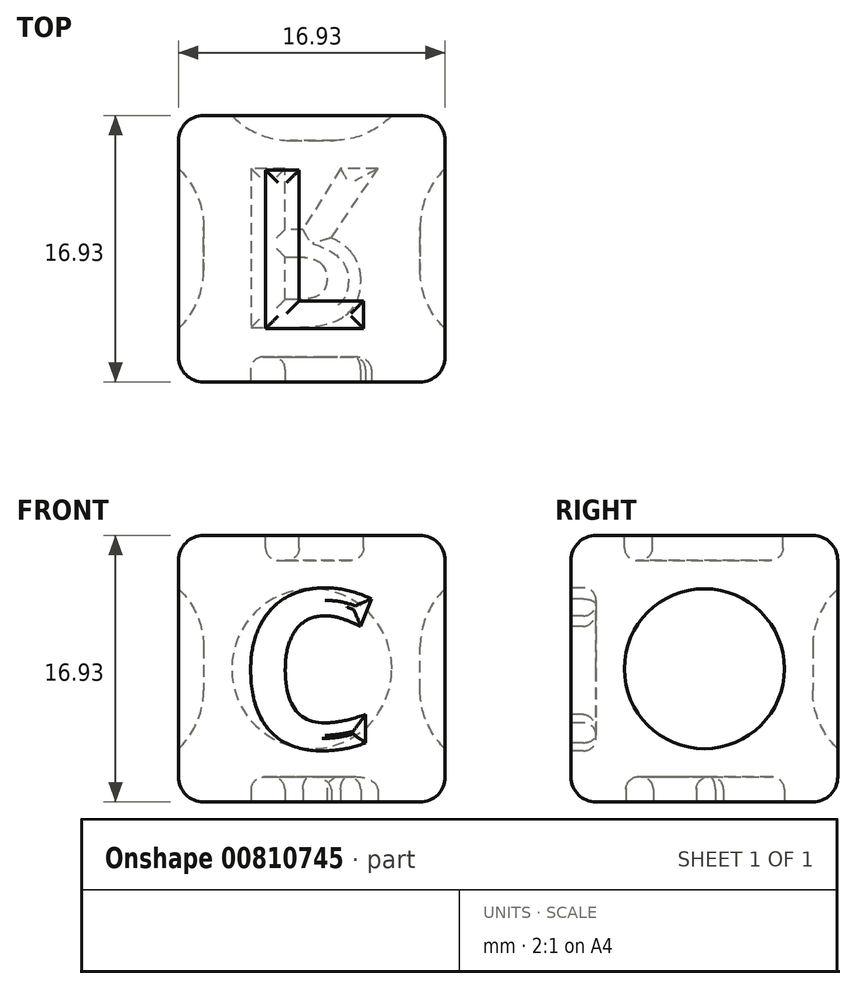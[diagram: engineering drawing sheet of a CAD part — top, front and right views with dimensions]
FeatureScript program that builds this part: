
annotation { "Feature Type Name" : "Feature", "Feature Type Description" : "" }
export const myFeature = defineFeature(function(context is Context, id is Id, definition is map)
    precondition{}
    {
        {
            var Q0;
            Q0=qCreatedBy(makeId("Top.planeOp"),FACE);
            var sketch = newSketch(context, id + "F0", { "sketchPlane" : qUnion([Q0])});
            skLineSegment(sketch, "E0.bottom", {"start": v(0, 0) * mm, "end": v(16.93, 0) * mm});
            skLineSegment(sketch, "E0.top", {"start": v(0, 16.93) * mm, "end": v(16.93, 16.93) * mm});
            skLineSegment(sketch, "E0.left", {"start": v(0, 0) * mm, "end": v(0, 16.93) * mm});
            skLineSegment(sketch, "E0.right", {"start": v(16.93, 0) * mm, "end": v(16.93, 16.93) * mm});
            skSolve(sketch);
        }
        {
            var Q0;
            Q0 = qSketchRegion(id + "F0", true);
            extrude(context, id + "F1", {"entities" : qUnion([Q0]), "depth" : 16.93 * mm, "offsetDistance" : 25.4 * mm});
        }
        {
            var Q0;
            Q0=makeQuery(id+"F1.opExtrude","CAP_EDGE",EDGE,{"disambiguationData":[OSD([sQuery(id+"F0.wireOp",EDGE,"E0.bottom")])],"isStart":false});
            var Q1;
            Q1=makeQuery(id+"F1.opExtrude","CAP_EDGE",EDGE,{"disambiguationData":[OSD([sQuery(id+"F0.wireOp",EDGE,"E0.left")])],"isStart":false});
            var Q2;
            Q2=makeQuery(id+"F1.opExtrude","CAP_EDGE",EDGE,{"disambiguationData":[OSD([sQuery(id+"F0.wireOp",EDGE,"E0.top")])],"isStart":false});
            var Q3;
            Q3=makeQuery(id+"F1.opExtrude","CAP_EDGE",EDGE,{"disambiguationData":[OSD([sQuery(id+"F0.wireOp",EDGE,"E0.right")])],"isStart":false});
            var Q4;
            Q4=makeQuery(id+"F1.opExtrude","SWEPT_EDGE",EDGE,{"disambiguationData":[OSD([sQuery(id+"F0.wireOp",EDGE,"E0.bottom"),sQuery(id+"F0.wireOp",EDGE,"E0.left")])]});
            var Q5;
            Q5=makeQuery(id+"F1.opExtrude","SWEPT_EDGE",EDGE,{"disambiguationData":[OSD([sQuery(id+"F0.wireOp",EDGE,"E0.top"),sQuery(id+"F0.wireOp",EDGE,"E0.left")])]});
            var Q6;
            Q6=makeQuery(id+"F1.opExtrude","SWEPT_EDGE",EDGE,{"disambiguationData":[OSD([sQuery(id+"F0.wireOp",EDGE,"E0.bottom"),sQuery(id+"F0.wireOp",EDGE,"E0.right")])]});
            var Q7;
            Q7=makeQuery(id+"F1.opExtrude","SWEPT_EDGE",EDGE,{"disambiguationData":[OSD([sQuery(id+"F0.wireOp",EDGE,"E0.top"),sQuery(id+"F0.wireOp",EDGE,"E0.right")])]});
            var Q8;
            Q8=makeQuery(id+"F1.opExtrude","CAP_EDGE",EDGE,{"disambiguationData":[OSD([sQuery(id+"F0.wireOp",EDGE,"E0.right")])],"isStart":true});
            var Q9;
            Q9=makeQuery(id+"F1.opExtrude","CAP_EDGE",EDGE,{"disambiguationData":[OSD([sQuery(id+"F0.wireOp",EDGE,"E0.left")])],"isStart":true});
            var Q10;
            Q10=makeQuery(id+"F1.opExtrude","CAP_EDGE",EDGE,{"disambiguationData":[OSD([sQuery(id+"F0.wireOp",EDGE,"E0.bottom")])],"isStart":true});
            var Q11;
            Q11=makeQuery(id+"F1.opExtrude","CAP_EDGE",EDGE,{"disambiguationData":[OSD([sQuery(id+"F0.wireOp",EDGE,"E0.top")])],"isStart":true});
            fillet(context, id + "F2", {"entities" : qUnion([Q0, Q1, Q2, Q3, Q4, Q5, Q6, Q7, Q8, Q9, Q10, Q11]), "radius" : 1.59 * mm, "tangentPropagation" : true, "allowEdgeOverflow" : false});
        }
        {
            var Q0;
            Q0=makeQuery(id+"F1.opExtrude","CAP_FACE",FACE,{"disambiguationData":[OSD([sQuery(id+"F0.wireOp",EDGE,"E0.bottom"),sQuery(id+"F0.wireOp",EDGE,"E0.top"),sQuery(id+"F0.wireOp",EDGE,"E0.left"),sQuery(id+"F0.wireOp",EDGE,"E0.right")])],"isStart":false});
            var sketch = newSketch(context, id + "F3", { "sketchPlane" : qUnion([Q0])});
            skText(sketch, "E1", { "text": "L", "fontName": "NotoSans-Bold.ttf"});
            skLineSegment(sketch, "E2", {"start": v(1.59, 15.35) * mm, "end": v(15.35, 1.59) * mm, "construction": true});
            skPoint(sketch, "E3", {"position": v(8.47, 8.47) * mm});
            const initialGuessF3  = {"E1": [0.00426, 0.00339, 1, 0, 0.01016]};
            skSetInitialGuess(sketch, initialGuessF3);
            skSolve(sketch);
        }
        {
            var Q0;
            Q0 = qSketchRegion(id + "F3", true);
            extrude(context, id + "F4", {"entities" : qUnion([Q0]), "operationType" : NewBodyOperationType.REMOVE, "oppositeDirection" : true, "depth" : 1.59 * mm, "offsetDistance" : 25.4 * mm});
        }
        {
            var Q0;
            Q0=makeQuery(id+"F1.opExtrude","SWEPT_FACE",FACE,{"disambiguationData":[OSD([sQuery(id+"F0.wireOp",EDGE,"E0.bottom")])]});
            var sketch = newSketch(context, id + "F5", { "sketchPlane" : qUnion([Q0])});
            skText(sketch, "E4", { "text": "C", "fontName": "NotoSans-Bold.ttf"});
            skLineSegment(sketch, "E5", {"start": v(1.59, 15.35) * mm, "end": v(15.35, 1.59) * mm, "construction": true});
            skPoint(sketch, "E6", {"position": v(8.47, 8.47) * mm});
            const initialGuessF5  = {"E4": [0.00376, 0.00339, 1, 0, 0.01016]};
            skSetInitialGuess(sketch, initialGuessF5);
            skSolve(sketch);
        }
        {
            var Q0;
            Q0 = qSketchRegion(id + "F5", true);
            extrude(context, id + "F6", {"entities" : qUnion([Q0]), "operationType" : NewBodyOperationType.REMOVE, "oppositeDirection" : true, "depth" : 1.59 * mm, "offsetDistance" : 25.4 * mm});
        }
        {
            var Q0;
            Q0=makeQuery(id+"F1.opExtrude","CAP_FACE",FACE,{"disambiguationData":[OSD([sQuery(id+"F0.wireOp",EDGE,"E0.bottom"),sQuery(id+"F0.wireOp",EDGE,"E0.top"),sQuery(id+"F0.wireOp",EDGE,"E0.left"),sQuery(id+"F0.wireOp",EDGE,"E0.right")])],"isStart":true});
            var sketch = newSketch(context, id + "F7", { "sketchPlane" : qUnion([Q0])});
            skText(sketch, "E7", { "text": "R", "fontName": "NotoSans-Bold.ttf"});
            skLineSegment(sketch, "E8", {"start": v(1.59, -1.59) * mm, "end": v(15.35, -15.35) * mm, "construction": true});
            skPoint(sketch, "E9", {"position": v(8.47, -8.47) * mm});
            const initialGuessF7  = {"E7": [0.00335, -0.01355, 1, 0, 0.01016]};
            skSetInitialGuess(sketch, initialGuessF7);
            skSolve(sketch);
        }
        {
            var Q0;
            Q0 = qSketchRegion(id + "F7", true);
            extrude(context, id + "F8", {"entities" : qUnion([Q0]), "operationType" : NewBodyOperationType.REMOVE, "oppositeDirection" : true, "depth" : 1.59 * mm, "offsetDistance" : 25.4 * mm});
        }
        {
            var Q0;
            Q0=makeQuery(id+"F1.opExtrude","SWEPT_FACE",FACE,{"disambiguationData":[OSD([sQuery(id+"F0.wireOp",EDGE,"E0.left")])]});
            var sketch = newSketch(context, id + "F9", { "sketchPlane" : qUnion([Q0])});
            skLineSegment(sketch, "E10", {"start": v(-15.35, 15.35) * mm, "end": v(-1.59, 1.59) * mm, "construction": true});
            skCircle(sketch, "E11", {"center": v(-8.47, 8.47) * mm, "radius": 5.08 * mm});
            skSolve(sketch);
        }
        {
            var Q0;
            Q0 = qSketchRegion(id + "F9", true);
            extrude(context, id + "F10", {"entities" : qUnion([Q0]), "operationType" : NewBodyOperationType.REMOVE, "oppositeDirection" : true, "depth" : 1.59 * mm, "offsetDistance" : 25.4 * mm});
        }
        {
            var Q0;
            Q0=makeQuery(id+"F1.opExtrude","SWEPT_FACE",FACE,{"disambiguationData":[OSD([sQuery(id+"F0.wireOp",EDGE,"E0.top")])]});
            var sketch = newSketch(context, id + "F11", { "sketchPlane" : qUnion([Q0])});
            skLineSegment(sketch, "E12", {"start": v(-15.35, 15.35) * mm, "end": v(-1.59, 1.59) * mm, "construction": true});
            skCircle(sketch, "E13", {"center": v(-8.47, 8.47) * mm, "radius": 5.08 * mm});
            skSolve(sketch);
        }
        {
            var Q0;
            Q0 = qSketchRegion(id + "F11", true);
            extrude(context, id + "F12", {"entities" : qUnion([Q0]), "operationType" : NewBodyOperationType.REMOVE, "oppositeDirection" : true, "depth" : 1.59 * mm, "offsetDistance" : 25.4 * mm});
        }
        {
            var Q0;
            Q0=makeQuery(id+"F1.opExtrude","SWEPT_FACE",FACE,{"disambiguationData":[OSD([sQuery(id+"F0.wireOp",EDGE,"E0.right")])]});
            var sketch = newSketch(context, id + "F13", { "sketchPlane" : qUnion([Q0])});
            skLineSegment(sketch, "E14", {"start": v(1.59, 15.35) * mm, "end": v(15.35, 1.59) * mm, "construction": true});
            skCircle(sketch, "E15", {"center": v(8.47, 8.47) * mm, "radius": 5.08 * mm});
            skSolve(sketch);
        }
        {
            var Q0;
            Q0 = qSketchRegion(id + "F13", true);
            extrude(context, id + "F14", {"entities" : qUnion([Q0]), "operationType" : NewBodyOperationType.REMOVE, "oppositeDirection" : true, "depth" : 1.59 * mm, "offsetDistance" : 25.4 * mm});
        }
        {
            var Q0;
            Q0=makeQuery(id+"F4.boolean.opBoolean","COPY",EDGE,{"derivedFrom":makeQuery(id+"F4.opExtrude","CAP_EDGE",EDGE,{"disambiguationData":[OSD([sQuery(id+"F3.wireOp",EDGE,"E1.sketch_text.stroke-2")])],"isStart":false})});
            var Q1;
            Q1=makeQuery(id+"F4.boolean.opBoolean","COPY",EDGE,{"derivedFrom":makeQuery(id+"F4.opExtrude","CAP_EDGE",EDGE,{"disambiguationData":[OSD([sQuery(id+"F3.wireOp",EDGE,"E1.sketch_text.stroke-0")])],"isStart":false})});
            var Q2;
            Q2=makeQuery(id+"F4.boolean.opBoolean","COPY",EDGE,{"derivedFrom":makeQuery(id+"F4.opExtrude","CAP_EDGE",EDGE,{"disambiguationData":[OSD([sQuery(id+"F3.wireOp",EDGE,"E1.sketch_text.stroke-3")])],"isStart":false})});
            var Q3;
            Q3=makeQuery(id+"F4.boolean.opBoolean","COPY",EDGE,{"derivedFrom":makeQuery(id+"F4.opExtrude","CAP_EDGE",EDGE,{"disambiguationData":[OSD([sQuery(id+"F3.wireOp",EDGE,"E1.sketch_text.stroke-5")])],"isStart":false})});
            var Q4;
            Q4=makeQuery(id+"F4.boolean.opBoolean","COPY",EDGE,{"derivedFrom":makeQuery(id+"F4.opExtrude","CAP_EDGE",EDGE,{"disambiguationData":[OSD([sQuery(id+"F3.wireOp",EDGE,"E1.sketch_text.stroke-4")])],"isStart":false})});
            var Q5;
            Q5=makeQuery(id+"F4.boolean.opBoolean","COPY",EDGE,{"derivedFrom":makeQuery(id+"F4.opExtrude","CAP_EDGE",EDGE,{"disambiguationData":[OSD([sQuery(id+"F3.wireOp",EDGE,"E1.sketch_text.stroke-1")])],"isStart":false})});
            var Q6;
            Q6=makeQuery(id+"F6.boolean.opBoolean","COPY",EDGE,{"derivedFrom":makeQuery(id+"F6.opExtrude","CAP_EDGE",EDGE,{"disambiguationData":[OSD([sQuery(id+"F5.wireOp",EDGE,"E4.sketch_text.stroke-10")])],"isStart":false})});
            var Q7;
            Q7=makeQuery(id+"F6.boolean.opBoolean","COPY",EDGE,{"derivedFrom":makeQuery(id+"F6.opExtrude","CAP_EDGE",EDGE,{"disambiguationData":[OSD([sQuery(id+"F5.wireOp",EDGE,"E4.sketch_text.stroke-0")])],"isStart":false})});
            var Q8;
            Q8=makeQuery(id+"F6.boolean.opBoolean","COPY",EDGE,{"derivedFrom":makeQuery(id+"F6.opExtrude","CAP_EDGE",EDGE,{"disambiguationData":[OSD([sQuery(id+"F5.wireOp",EDGE,"E4.sketch_text.stroke-12")])],"isStart":false})});
            var Q9;
            Q9=makeQuery(id+"F6.boolean.opBoolean","COPY",EDGE,{"derivedFrom":makeQuery(id+"F6.opExtrude","CAP_EDGE",EDGE,{"disambiguationData":[OSD([sQuery(id+"F5.wireOp",EDGE,"E4.sketch_text.stroke-4")])],"isStart":false})});
            var Q10;
            Q10=makeQuery(id+"F8.boolean.opBoolean","COPY",EDGE,{"derivedFrom":makeQuery(id+"F8.opExtrude","CAP_EDGE",EDGE,{"disambiguationData":[OSD([sQuery(id+"F7.wireOp",EDGE,"E7.sketch_text.stroke-11")])],"isStart":false})});
            var Q11;
            Q11=makeQuery(id+"F8.boolean.opBoolean","COPY",EDGE,{"derivedFrom":makeQuery(id+"F8.opExtrude","CAP_EDGE",EDGE,{"disambiguationData":[OSD([sQuery(id+"F7.wireOp",EDGE,"E7.sketch_text.stroke-15")])],"isStart":false})});
            var Q12;
            Q12=makeQuery(id+"F8.boolean.opBoolean","COPY",EDGE,{"derivedFrom":makeQuery(id+"F8.opExtrude","CAP_EDGE",EDGE,{"disambiguationData":[OSD([sQuery(id+"F7.wireOp",EDGE,"E7.sketch_text.stroke-1")])],"isStart":false})});
            var Q13;
            Q13=makeQuery(id+"F8.boolean.opBoolean","COPY",EDGE,{"derivedFrom":makeQuery(id+"F8.opExtrude","CAP_EDGE",EDGE,{"disambiguationData":[OSD([sQuery(id+"F7.wireOp",EDGE,"E7.sketch_text.stroke-6")])],"isStart":false})});
            var Q14;
            Q14=makeQuery(id+"F8.boolean.opBoolean","COPY",EDGE,{"derivedFrom":makeQuery(id+"F8.opExtrude","CAP_EDGE",EDGE,{"disambiguationData":[OSD([sQuery(id+"F7.wireOp",EDGE,"E7.sketch_text.stroke-9")])],"isStart":false})});
            var Q15;
            Q15=makeQuery(id+"F8.boolean.opBoolean","COPY",EDGE,{"derivedFrom":makeQuery(id+"F8.opExtrude","CAP_EDGE",EDGE,{"disambiguationData":[OSD([sQuery(id+"F7.wireOp",EDGE,"E7.sketch_text.stroke-8")])],"isStart":false})});
            var Q16;
            Q16=makeQuery(id+"F8.boolean.opBoolean","COPY",EDGE,{"derivedFrom":makeQuery(id+"F8.opExtrude","CAP_EDGE",EDGE,{"disambiguationData":[OSD([sQuery(id+"F7.wireOp",EDGE,"E7.sketch_text.stroke-7")])],"isStart":false})});
            var Q17;
            Q17=makeQuery(id+"F8.boolean.opBoolean","COPY",EDGE,{"derivedFrom":makeQuery(id+"F8.opExtrude","CAP_EDGE",EDGE,{"disambiguationData":[OSD([sQuery(id+"F7.wireOp",EDGE,"E7.sketch_text.stroke-16")])],"isStart":false})});
            var Q18;
            Q18=makeQuery(id+"F8.boolean.opBoolean","COPY",EDGE,{"derivedFrom":makeQuery(id+"F8.opExtrude","CAP_EDGE",EDGE,{"disambiguationData":[OSD([sQuery(id+"F7.wireOp",EDGE,"E7.sketch_text.stroke-17")])],"isStart":false})});
            var Q19;
            Q19=makeQuery(id+"F8.boolean.opBoolean","COPY",EDGE,{"derivedFrom":makeQuery(id+"F8.opExtrude","CAP_EDGE",EDGE,{"disambiguationData":[OSD([sQuery(id+"F7.wireOp",EDGE,"E7.sketch_text.stroke-18")])],"isStart":false})});
            fillet(context, id + "F15", {"entities" : qUnion([Q0, Q1, Q2, Q3, Q4, Q5, Q6, Q7, Q8, Q9, Q10, Q11, Q12, Q13, Q14, Q15, Q16, Q17, Q18, Q19]), "radius" : 0.8 * mm, "tangentPropagation" : true, "allowEdgeOverflow" : false});
        }
        {
            var Q0;
            Q0=makeQuery(id+"F12.boolean.opBoolean","COPY",EDGE,{"derivedFrom":makeQuery(id+"F12.opExtrude","CAP_EDGE",EDGE,{"disambiguationData":[OSD([sQuery(id+"F11.wireOp",EDGE,"E13")])],"isStart":false})});
            var Q1;
            Q1=makeQuery(id+"F14.boolean.opBoolean","COPY",EDGE,{"derivedFrom":makeQuery(id+"F14.opExtrude","CAP_EDGE",EDGE,{"disambiguationData":[OSD([sQuery(id+"F13.wireOp",EDGE,"E15")])],"isStart":false})});
            var Q2;
            Q2=makeQuery(id+"F10.boolean.opBoolean","COPY",EDGE,{"derivedFrom":makeQuery(id+"F10.opExtrude","CAP_EDGE",EDGE,{"disambiguationData":[OSD([sQuery(id+"F9.wireOp",EDGE,"E11")])],"isStart":false})});
            fillet(context, id + "F16", {"entities" : qUnion([Q0, Q1, Q2]), "radius" : 5.08 * mm, "tangentPropagation" : true, "allowEdgeOverflow" : false});
        }
    });
